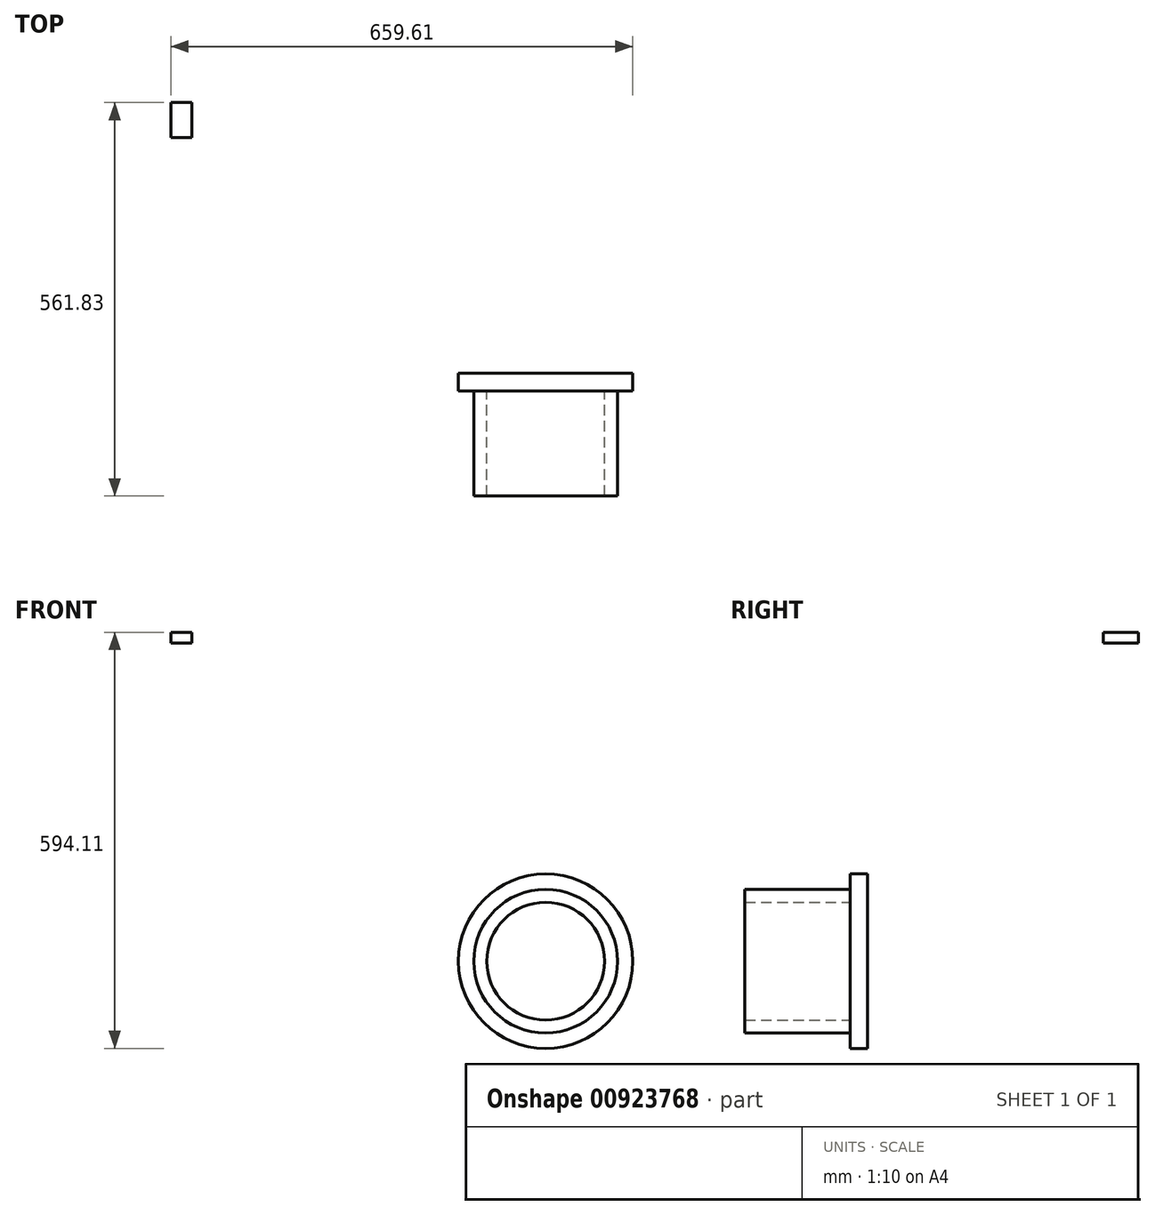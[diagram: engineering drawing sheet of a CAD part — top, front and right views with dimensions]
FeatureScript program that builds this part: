
annotation { "Feature Type Name" : "Feature", "Feature Type Description" : "" }
export const myFeature = defineFeature(function(context is Context, id is Id, definition is map)
    precondition{}
    {
        {
            var Q0;
            Q0=qCreatedBy(makeId("Top.planeOp"),FACE);
            var sketch = newSketch(context, id + "F0", { "sketchPlane" : qUnion([Q0])});
            skLineSegment(sketch, "E0", {"start": v(1105.95, -517.68) * mm, "end": v(1105.95, -1101.52) * mm});
            skLineSegment(sketch, "E1", {"start": v(1105.95, -1101.52) * mm, "end": v(1647.17, -1101.52) * mm});
            skLineSegment(sketch, "E2", {"start": v(1647.17, -1101.52) * mm, "end": v(1647.17, -521.94) * mm});
            skLineSegment(sketch, "E3", {"start": v(1105.95, -517.68) * mm, "end": v(1647.17, -521.94) * mm});
            skLineSegment(sketch, "E4", {"start": v(-423.97, -555.32) * mm, "end": v(0, -806.76) * mm});
            skLineSegment(sketch, "E5", {"start": v(0, -806.76) * mm, "end": v(556.2, -806.76) * mm});
            skLineSegment(sketch, "E6", {"start": v(962.54, 708.16) * mm, "end": v(1087.67, 402.8) * mm});
            skLineSegment(sketch, "E7", {"start": v(1087.67, 402.8) * mm, "end": v(1547.65, 402.8) * mm});
            skLineSegment(sketch, "E8", {"start": v(1547.65, 402.8) * mm, "end": v(962.54, 708.16) * mm});
            skLineSegment(sketch, "E9", {"start": v(-1588.38, 411.83) * mm, "end": v(-1588.38, 361.83) * mm});
            skLineSegment(sketch, "E10", {"start": v(-1588.38, 411.83) * mm, "end": v(-1558.38, 411.83) * mm});
            skLineSegment(sketch, "E11", {"start": v(-1558.38, 411.83) * mm, "end": v(-1558.38, 361.83) * mm});
            skLineSegment(sketch, "E12", {"start": v(-1558.38, 361.83) * mm, "end": v(-1588.38, 361.83) * mm});
            skSolve(sketch);
        }
        {
            var Q0;
            Q0=makeQuery(id+"F0.imprint","IMPRINT",FACE,{"disambiguationData":[TD([[makeQuery(id+"F0.imprint","IMPRINT",EDGE,{"derivedFrom":sQuery(id+"F0.wireOp",EDGE,"E9")}),1.0]])]});
            extrude(context, id + "F1", {"entities" : qUnion([Q0]), "depth" : 15 * mm, "offsetDistance" : 25 * mm});
        }
        {
            var Q0;
            Q0=qCreatedBy(makeId("Front.planeOp"),FACE);
            var sketch = newSketch(context, id + "F2", { "sketchPlane" : qUnion([Q0])});
            skCircle(sketch, "E13", {"center": v(-1053.27, -454.6) * mm, "radius": 102.65 * mm});
            skCircle(sketch, "E14", {"center": v(-1053.27, -454.6) * mm, "radius": 84.1 * mm});
            skSolve(sketch);
        }
        {
            var Q0;
            Q0=makeQuery(id+"F2.imprint","IMPRINT",FACE,{"disambiguationData":[TD([[makeQuery(id+"F2.imprint","IMPRINT",EDGE,{"derivedFrom":sQuery(id+"F2.wireOp",EDGE,"E13")}),1.0]])]});
            extrude(context, id + "F3", {"entities" : qUnion([Q0]), "depth" : 150 * mm, "offsetDistance" : 25 * mm});
        }
        {
            var Q0;
            Q0=makeQuery(id+"F3.opExtrude","CAP_FACE",FACE,{"disambiguationData":[OSD([sQuery(id+"F2.wireOp",EDGE,"E13"),sQuery(id+"F2.wireOp",EDGE,"E14")])],"isStart":true});
            var sketch = newSketch(context, id + "F4", { "sketchPlane" : qUnion([Q0])});
            skCircle(sketch, "E15", {"center": v(1053.27, -454.6) * mm, "radius": 124.5 * mm});
            skSolve(sketch);
        }
        {
            var Q0;
            Q0=makeQuery(id+"F4.imprint","IMPRINT",FACE,{"disambiguationData":[TD([[makeQuery(id+"F4.imprint","IMPRINT",EDGE,{"derivedFrom":sQuery(id+"F4.wireOp",EDGE,"E15")}),1.0]])]});
            var Q1;
            Q1=makeQuery(id+"F4.imprint","IMPRINT",FACE,{"disambiguationData":[TD([[makeQuery(id+"F4.imprint","IMPRINT",EDGE,{"derivedFrom":makeQuery(id+"F3.opExtrude","CAP_EDGE",EDGE,{"disambiguationData":[OSD([sQuery(id+"F2.wireOp",EDGE,"E13")])],"isStart":true})}),-1.0]])]});
            var Q2;
            Q2=makeQuery(id+"F4.imprint","IMPRINT",FACE,{"disambiguationData":[TD([[makeQuery(id+"F4.imprint","IMPRINT",EDGE,{"derivedFrom":makeQuery(id+"F3.opExtrude","CAP_EDGE",EDGE,{"disambiguationData":[OSD([sQuery(id+"F2.wireOp",EDGE,"E14")])],"isStart":true})}),-1.0]])]});
            extrude(context, id + "F5", {"entities" : qUnion([Q0, Q1, Q2]), "operationType" : NewBodyOperationType.ADD, "depth" : 25 * mm, "offsetDistance" : 25 * mm});
        }
    });
